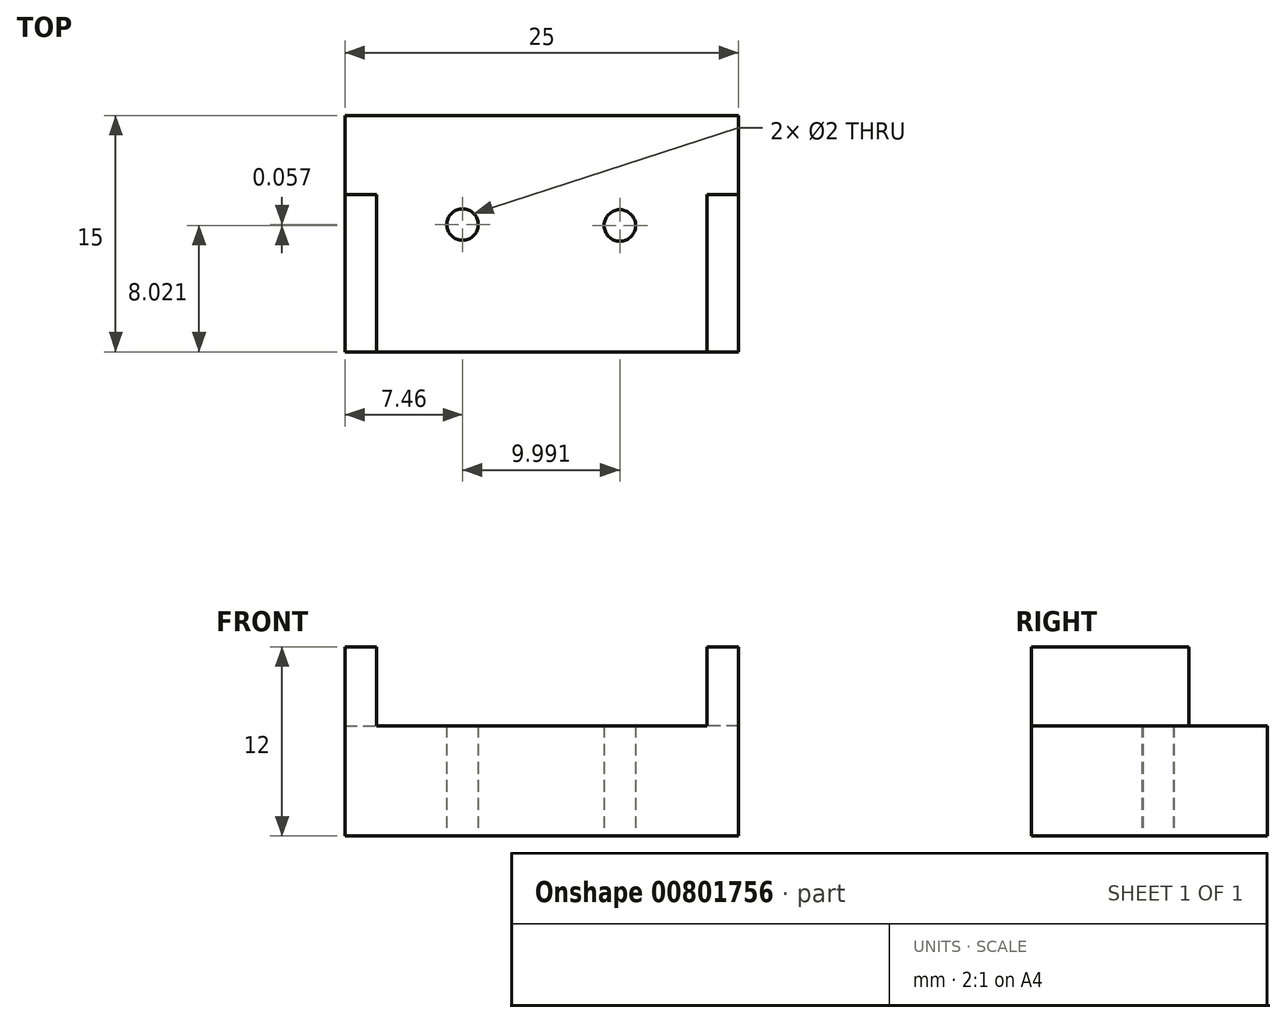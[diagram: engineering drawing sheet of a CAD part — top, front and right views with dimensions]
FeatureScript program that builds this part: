
annotation { "Feature Type Name" : "Feature", "Feature Type Description" : "" }
export const myFeature = defineFeature(function(context is Context, id is Id, definition is map)
    precondition{}
    {
        {
            var Q0;
            Q0=qCreatedBy(makeId("Top.planeOp"),FACE);
            var sketch = newSketch(context, id + "F0", { "sketchPlane" : qUnion([Q0])});
            skLineSegment(sketch, "E0.bottom", {"start": v(0, 0) * mm, "end": v(25, 0) * mm});
            skLineSegment(sketch, "E0.top", {"start": v(0, 15) * mm, "end": v(25, 15) * mm});
            skLineSegment(sketch, "E0.left", {"start": v(0, 0) * mm, "end": v(0, 15) * mm});
            skLineSegment(sketch, "E0.right", {"start": v(25, 0) * mm, "end": v(25, 15) * mm});
            skSolve(sketch);
        }
        {
            var Q0;
            Q0=makeQuery(id+"F0.imprint","IMPRINT",FACE,{"disambiguationData":[TD([[makeQuery(id+"F0.imprint","IMPRINT",EDGE,{"derivedFrom":sQuery(id+"F0.wireOp",EDGE,"E0.bottom")}),1.0]])]});
            extrude(context, id + "F1", {"entities" : qUnion([Q0]), "depth" : 7 * mm, "offsetDistance" : 25 * mm});
        }
        {
            var Q0;
            Q0=makeQuery(id+"F1.opExtrude","CAP_FACE",FACE,{"disambiguationData":[OSD([sQuery(id+"F0.wireOp",EDGE,"E0.bottom"),sQuery(id+"F0.wireOp",EDGE,"E0.top"),sQuery(id+"F0.wireOp",EDGE,"E0.left"),sQuery(id+"F0.wireOp",EDGE,"E0.right")])],"isStart":false});
            var sketch = newSketch(context, id + "F2", { "sketchPlane" : qUnion([Q0])});
            skSolve(sketch);
        }
        {
            var Q0;
            Q0=makeQuery(id+"F2.imprint","IMPRINT",FACE,{"disambiguationData":[TD([[makeQuery(id+"F2.imprint","IMPRINT",EDGE,{"derivedFrom":makeQuery(id+"F1.opExtrude","CAP_EDGE",EDGE,{"disambiguationData":[OSD([sQuery(id+"F0.wireOp",EDGE,"E0.bottom")])],"isStart":false})}),1.0]])]});
            var sketch = newSketch(context, id + "F3", { "sketchPlane" : qUnion([Q0])});
            skLineSegment(sketch, "E1.bottom", {"start": v(0, 0) * mm, "end": v(2, 0) * mm});
            skLineSegment(sketch, "E1.top", {"start": v(0, 10) * mm, "end": v(2, 10) * mm});
            skLineSegment(sketch, "E1.left", {"start": v(0, 0) * mm, "end": v(0, 10) * mm});
            skLineSegment(sketch, "E1.right", {"start": v(2, 0) * mm, "end": v(2, 10) * mm});
            skSolve(sketch);
        }
        {
            var Q0;
            Q0 = qSketchRegion(id + "F3", true);
            extrude(context, id + "F4", {"entities" : qUnion([Q0]), "operationType" : NewBodyOperationType.ADD, "depth" : 5 * mm, "offsetDistance" : 25 * mm});
        }
        {
            var Q0;
            Q0=makeQuery(id+"F2.imprint","IMPRINT",FACE,{"disambiguationData":[TD([[makeQuery(id+"F2.imprint","IMPRINT",EDGE,{"derivedFrom":makeQuery(id+"F1.opExtrude","CAP_EDGE",EDGE,{"disambiguationData":[OSD([sQuery(id+"F0.wireOp",EDGE,"E0.bottom")])],"isStart":false})}),1.0]])]});
            var sketch = newSketch(context, id + "F5", { "sketchPlane" : qUnion([Q0])});
            skLineSegment(sketch, "E2.bottom", {"start": v(24.98, 0) * mm, "end": v(22.98, 0) * mm});
            skLineSegment(sketch, "E2.top", {"start": v(24.98, 10) * mm, "end": v(22.98, 10) * mm});
            skLineSegment(sketch, "E2.left", {"start": v(24.98, 0) * mm, "end": v(24.98, 10) * mm});
            skLineSegment(sketch, "E2.right", {"start": v(22.98, 0) * mm, "end": v(22.98, 10) * mm});
            skSolve(sketch);
        }
        {
            var Q0;
            Q0 = qSketchRegion(id + "F5", true);
            extrude(context, id + "F6", {"entities" : qUnion([Q0]), "operationType" : NewBodyOperationType.ADD, "depth" : 5 * mm, "offsetDistance" : 25 * mm});
        }
        {
            var Q0;
            Q0=makeQuery(id+"F2.imprint","IMPRINT",FACE,{"disambiguationData":[TD([[makeQuery(id+"F2.imprint","IMPRINT",EDGE,{"derivedFrom":makeQuery(id+"F1.opExtrude","CAP_EDGE",EDGE,{"disambiguationData":[OSD([sQuery(id+"F0.wireOp",EDGE,"E0.bottom")])],"isStart":false})}),1.0]])]});
            var sketch = newSketch(context, id + "F7", { "sketchPlane" : qUnion([Q0])});
            skLineSegment(sketch, "E3.bottom", {"start": v(2.45, 10.02) * mm, "end": v(22.45, 10.02) * mm});
            skLineSegment(sketch, "E3.top", {"start": v(2.45, 8.02) * mm, "end": v(22.45, 8.02) * mm});
            skLineSegment(sketch, "E3.left", {"start": v(2.45, 10.02) * mm, "end": v(2.45, 8.02) * mm});
            skLineSegment(sketch, "E3.right", {"start": v(22.45, 10.02) * mm, "end": v(22.45, 8.02) * mm});
            skLineSegment(sketch, "E4.bottom", {"start": v(2.45, 10.02) * mm, "end": v(12.45, 10.02) * mm});
            skLineSegment(sketch, "E4.top", {"start": v(2.45, 8.02) * mm, "end": v(12.45, 8.02) * mm});
            skLineSegment(sketch, "E4.right", {"start": v(12.45, 10.02) * mm, "end": v(12.45, 8.02) * mm});
            skLineSegment(sketch, "E5.bottom", {"start": v(12.45, 10.02) * mm, "end": v(7.45, 10.02) * mm});
            skLineSegment(sketch, "E5.top", {"start": v(12.45, 8.02) * mm, "end": v(7.45, 8.02) * mm});
            skLineSegment(sketch, "E5.right", {"start": v(7.45, 10.02) * mm, "end": v(7.45, 8.02) * mm});
            skLineSegment(sketch, "E6.bottom", {"start": v(12.45, 10.02) * mm, "end": v(17.45, 10.02) * mm});
            skLineSegment(sketch, "E6.top", {"start": v(12.45, 8.02) * mm, "end": v(17.45, 8.02) * mm});
            skLineSegment(sketch, "E6.right", {"start": v(17.45, 10.02) * mm, "end": v(17.45, 8.02) * mm});
            skSolve(sketch);
        }
        {
            var Q0;
            Q0=makeQuery(id+"F2.imprint","IMPRINT",FACE,{"disambiguationData":[TD([[makeQuery(id+"F2.imprint","IMPRINT",EDGE,{"derivedFrom":makeQuery(id+"F1.opExtrude","CAP_EDGE",EDGE,{"disambiguationData":[OSD([sQuery(id+"F0.wireOp",EDGE,"E0.bottom")])],"isStart":false})}),1.0]])]});
            var sketch = newSketch(context, id + "F8", { "sketchPlane" : qUnion([Q0])});
            skCircle(sketch, "E7", {"center": v(7.46, 8.08) * mm, "radius": 1 * mm});
            skCircle(sketch, "E8", {"center": v(17.42, 8.08) * mm, "radius": 1 * mm});
            skSolve(sketch);
        }
        {
            var Q0;
            Q0=sQuery(id+"F8.wireOp",VERTEX,"E7.center");
            var Q1;
            Q1=sQuery(id+"F7.wireOp",VERTEX,"E6.top.end");
            var Q2;
            Q2=makeQuery(id+"F1.opExtrude","SWEPT_BODY",BODY,{"disambiguationData":[OSD([sQuery(id+"F0.wireOp",EDGE,"E0.bottom"),sQuery(id+"F0.wireOp",EDGE,"E0.top"),sQuery(id+"F0.wireOp",EDGE,"E0.left"),sQuery(id+"F0.wireOp",EDGE,"E0.right")])]});
            hole(context, id + "F9", {"style" : HoleStyle.SIMPLE, "endStyle" : HoleEndStyle.THROUGH, "holeDiameter" : 2 * mm, "majorDiameter" : 5 * mm, "isTappedThrough" : true, "tappedDepth" : 12 * mm, "tapClearance" : 3, "startFromSketch" : true, "locations" : qUnion([Q0, Q1]), "scope" : qUnion([Q2])});
        }
    });
